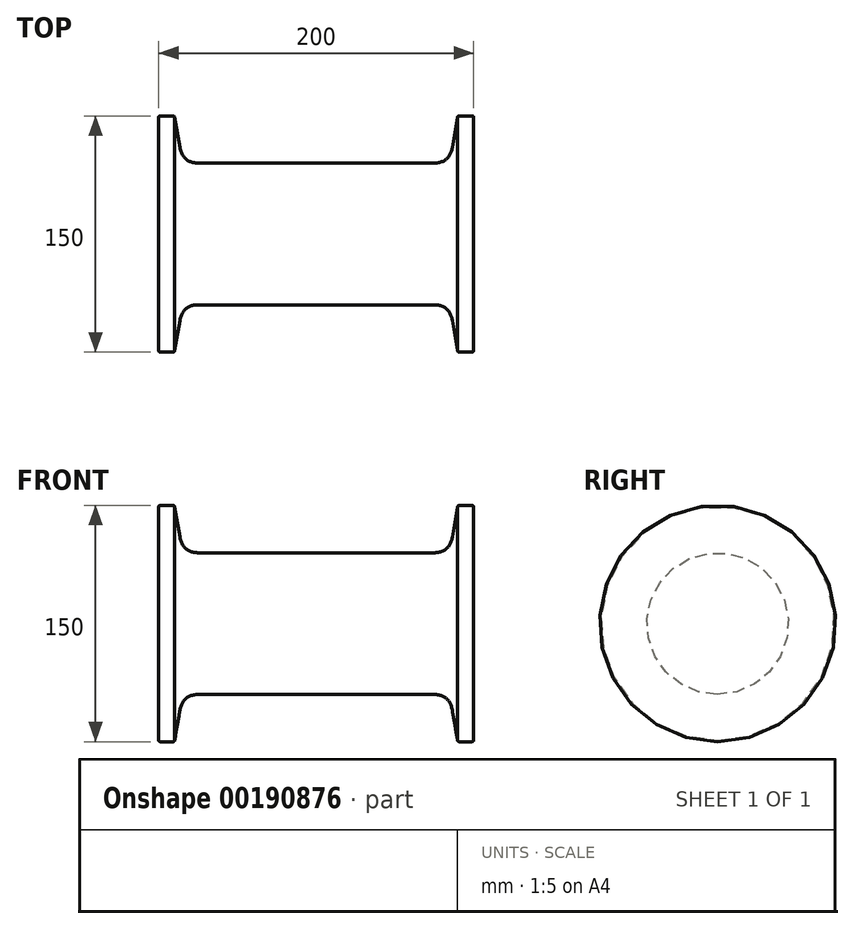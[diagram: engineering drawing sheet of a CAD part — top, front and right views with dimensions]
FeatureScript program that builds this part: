
annotation { "Feature Type Name" : "Feature", "Feature Type Description" : "" }
export const myFeature = defineFeature(function(context is Context, id is Id, definition is map)
    precondition{}
    {
        {
            var Q0;
            Q0=qCreatedBy(makeId("Front.planeOp"),FACE);
            var sketch = newSketch(context, id + "F0", { "sketchPlane" : qUnion([Q0])});
            skLineSegment(sketch, "E0", {"start": v(-100, 0) * mm, "end": v(-100, 75) * mm});
            skLineSegment(sketch, "E1", {"start": v(-100, 75) * mm, "end": v(-90, 75) * mm});
            skLineSegment(sketch, "E2", {"start": v(-90, 75) * mm, "end": v(-84.71, 45) * mm});
            skLineSegment(sketch, "E3", {"start": v(-84.71, 45) * mm, "end": v(0, 45) * mm});
            skLineSegment(sketch, "E4", {"start": v(0, 45) * mm, "end": v(0, 0) * mm});
            skLineSegment(sketch, "E5", {"start": v(0, 0) * mm, "end": v(-100, 0) * mm});
            skSolve(sketch);
        }
        {
            var Q0;
            Q0=makeQuery(id+"F0.imprint","IMPRINT",FACE,{"disambiguationData":[TD([[makeQuery(id+"F0.imprint","IMPRINT",EDGE,{"derivedFrom":sQuery(id+"F0.wireOp",EDGE,"E0")}),-1.0]])]});
            var Q1;
            Q1=sQuery(id+"F0.wireOp",EDGE,"E5");
            revolve(context, id + "F1", {"surfaceOperationType" : NewSurfaceOperationType.NEW, "entities" : qUnion([Q0]), "axis" : qUnion([Q1]), "revolveType" : RevolveType.FULL});
        }
        {
            var Q0;
            Q0=makeQuery(id+"F1.opRevolve","SWEPT_BODY",BODY,{"disambiguationData":[OSD([sQuery(id+"F0.wireOp",EDGE,"E0"),sQuery(id+"F0.wireOp",EDGE,"E1"),sQuery(id+"F0.wireOp",EDGE,"E2"),sQuery(id+"F0.wireOp",EDGE,"E3"),sQuery(id+"F0.wireOp",EDGE,"E4"),sQuery(id+"F0.wireOp",EDGE,"E5")])]});
            var Q1;
            Q1=makeQuery(id+"F1.opRevolve","SWEPT_FACE",FACE,{"disambiguationData":[OSD([sQuery(id+"F0.wireOp",EDGE,"E4")])]});
            mirror(context, id + "F2", {"operationType" : NewBodyOperationType.ADD, "entities" : qUnion([Q0]), "mirrorPlane" : qUnion([Q1])});
        }
        {
            var Q0;
            Q0=makeQuery(id+"F1.opRevolve","SWEPT_EDGE",EDGE,{"disambiguationData":[OSD([sQuery(id+"F0.wireOp",EDGE,"E2"),sQuery(id+"F0.wireOp",EDGE,"E3")])]});
            var Q1;
            Q1=makeQuery(id+"F2.opPattern","COPY",EDGE,{"derivedFrom":makeQuery(id+"F1.opRevolve","SWEPT_EDGE",EDGE,{"disambiguationData":[OSD([sQuery(id+"F0.wireOp",EDGE,"E2"),sQuery(id+"F0.wireOp",EDGE,"E3")])]}),"instanceName":"1"});
            fillet(context, id + "F3", {"entities" : qUnion([Q0, Q1]), "radius" : 12 * mm, "tangentPropagation" : true, "rho" : 0.5, "crossSection" : FilletCrossSection.CONIC, "allowEdgeOverflow" : false});
        }
        {
            var Q0;
            Q0=makeQuery(id+"F1.opRevolve","SWEPT_FACE",FACE,{"disambiguationData":[OSD([sQuery(id+"F0.wireOp",EDGE,"E1")])]});
            var Q1;
            Q1=makeQuery(id+"F2.opPattern","COPY",FACE,{"derivedFrom":makeQuery(id+"F1.opRevolve","SWEPT_FACE",FACE,{"disambiguationData":[OSD([sQuery(id+"F0.wireOp",EDGE,"E1")])]}),"instanceName":"1"});
            fillet(context, id + "F4", {"entities" : qUnion([Q0, Q1]), "radius" : 1 * mm, "tangentPropagation" : true, "rho" : 0.5, "crossSection" : FilletCrossSection.CONIC, "allowEdgeOverflow" : false});
        }
    });
